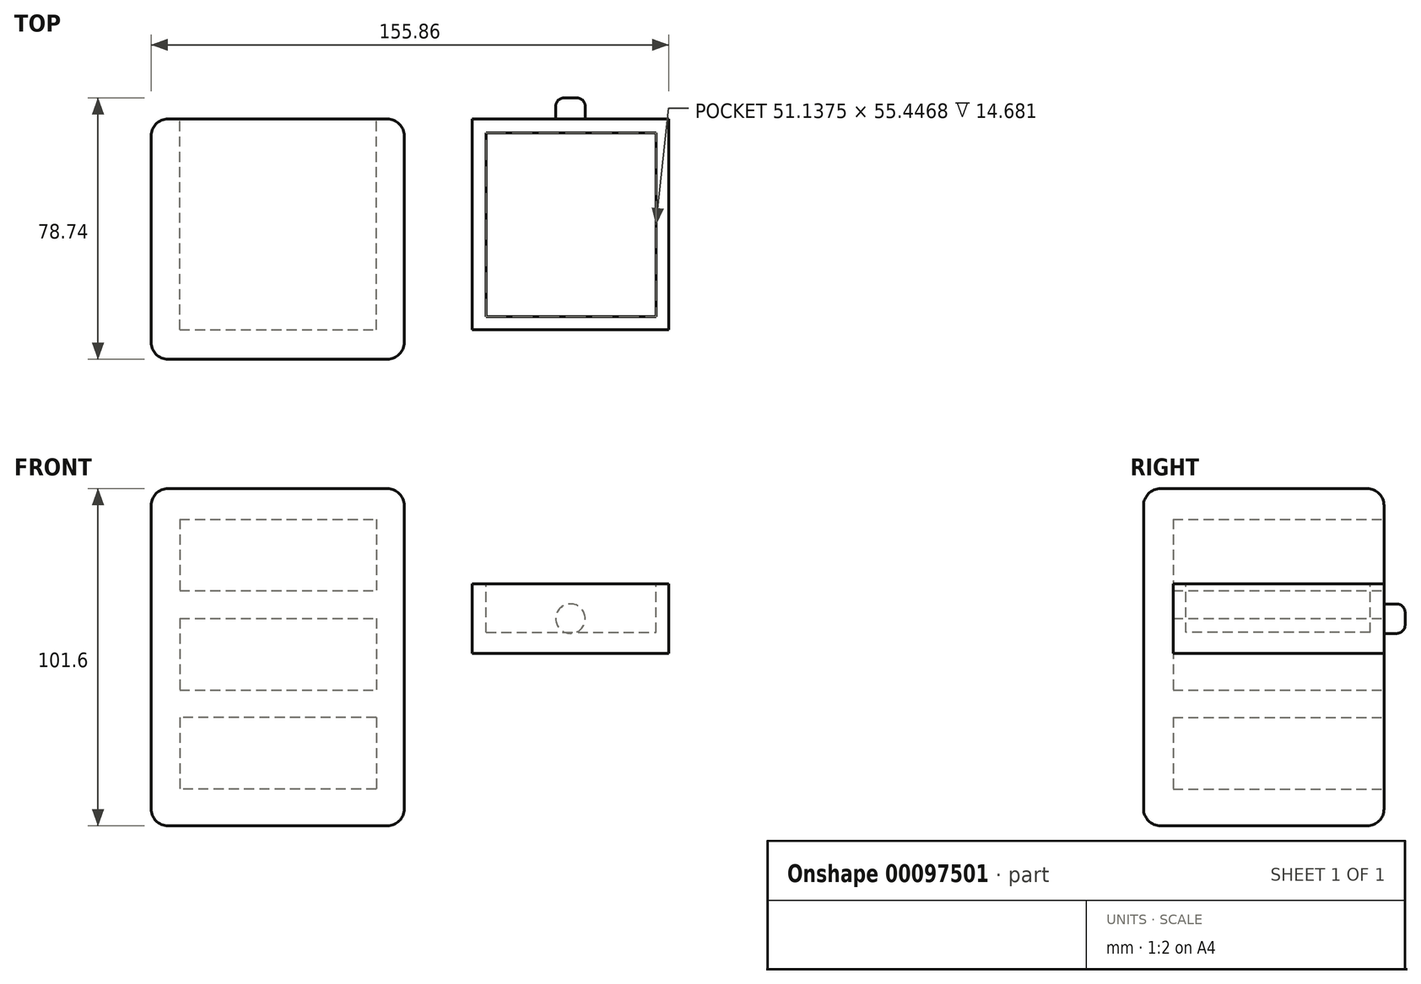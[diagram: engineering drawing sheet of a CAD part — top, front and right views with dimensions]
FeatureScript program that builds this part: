
annotation { "Feature Type Name" : "Feature", "Feature Type Description" : "" }
export const myFeature = defineFeature(function(context is Context, id is Id, definition is map)
    precondition{}
    {
        {
            var Q0;
            Q0=qCreatedBy(makeId("Front.planeOp"),FACE);
            var sketch = newSketch(context, id + "F0", { "sketchPlane" : qUnion([Q0])});
            skLineSegment(sketch, "E0.bottom", {"start": v(-38.24, 55.06) * mm, "end": v(37.96, 55.06) * mm});
            skLineSegment(sketch, "E0.top", {"start": v(-38.24, -46.54) * mm, "end": v(37.96, -46.54) * mm});
            skLineSegment(sketch, "E0.left", {"start": v(-38.24, 55.06) * mm, "end": v(-38.24, -46.54) * mm});
            skLineSegment(sketch, "E0.right", {"start": v(37.96, 55.06) * mm, "end": v(37.96, -46.54) * mm});
            skLineSegment(sketch, "E1.bottom", {"start": v(-29.6, 45.82) * mm, "end": v(29.6, 45.82) * mm});
            skLineSegment(sketch, "E1.top", {"start": v(-29.6, 24.28) * mm, "end": v(29.6, 24.28) * mm});
            skLineSegment(sketch, "E1.left", {"start": v(-29.6, 45.82) * mm, "end": v(-29.6, 24.28) * mm});
            skLineSegment(sketch, "E1.right", {"start": v(29.6, 45.82) * mm, "end": v(29.6, 24.28) * mm});
            skLineSegment(sketch, "E2.bottom", {"start": v(-29.6, 15.94) * mm, "end": v(29.6, 15.94) * mm});
            skLineSegment(sketch, "E2.top", {"start": v(-29.6, -5.6) * mm, "end": v(29.6, -5.6) * mm});
            skLineSegment(sketch, "E2.left", {"start": v(-29.6, 15.94) * mm, "end": v(-29.6, -5.6) * mm});
            skLineSegment(sketch, "E2.right", {"start": v(29.6, 15.94) * mm, "end": v(29.6, -5.6) * mm});
            skLineSegment(sketch, "E3.bottom", {"start": v(29.6, -13.93) * mm, "end": v(-29.6, -13.93) * mm});
            skLineSegment(sketch, "E3.top", {"start": v(29.6, -35.48) * mm, "end": v(-29.6, -35.48) * mm});
            skLineSegment(sketch, "E3.left", {"start": v(29.6, -13.93) * mm, "end": v(29.6, -35.48) * mm});
            skLineSegment(sketch, "E3.right", {"start": v(-29.6, -13.93) * mm, "end": v(-29.6, -35.48) * mm});
            skSolve(sketch);
        }
        {
            var Q0;
            Q0=makeQuery(id+"F0.imprint","IMPRINT",FACE,{"disambiguationData":[TD([[makeQuery(id+"F0.imprint","IMPRINT",EDGE,{"derivedFrom":sQuery(id+"F0.wireOp",EDGE,"E0.bottom")}),-1.0]])]});
            extrude(context, id + "F1", {"entities" : qUnion([Q0]), "depth" : 63.5 * mm});
        }
        {
            var Q0;
            Q0=makeQuery(id+"F1.opExtrude","CAP_FACE",FACE,{"disambiguationData":[OSD([sQuery(id+"F0.wireOp",EDGE,"E0.bottom"),sQuery(id+"F0.wireOp",EDGE,"E0.top"),sQuery(id+"F0.wireOp",EDGE,"E0.left"),sQuery(id+"F0.wireOp",EDGE,"E0.right"),sQuery(id+"F0.wireOp",EDGE,"E1.bottom"),sQuery(id+"F0.wireOp",EDGE,"E1.top"),sQuery(id+"F0.wireOp",EDGE,"E1.left"),sQuery(id+"F0.wireOp",EDGE,"E1.right"),sQuery(id+"F0.wireOp",EDGE,"E2.bottom"),sQuery(id+"F0.wireOp",EDGE,"E2.top"),sQuery(id+"F0.wireOp",EDGE,"E2.left"),sQuery(id+"F0.wireOp",EDGE,"E2.right"),sQuery(id+"F0.wireOp",EDGE,"E3.bottom"),sQuery(id+"F0.wireOp",EDGE,"E3.top"),sQuery(id+"F0.wireOp",EDGE,"E3.left"),sQuery(id+"F0.wireOp",EDGE,"E3.right")])],"isStart":false});
            var sketch = newSketch(context, id + "F2", { "sketchPlane" : qUnion([Q0])});
            skLineSegment(sketch, "E4.bottom", {"start": v(-38.24, 55.06) * mm, "end": v(37.96, 55.06) * mm});
            skLineSegment(sketch, "E4.top", {"start": v(-38.24, -46.54) * mm, "end": v(37.96, -46.54) * mm});
            skLineSegment(sketch, "E4.left", {"start": v(-38.24, 55.06) * mm, "end": v(-38.24, -46.54) * mm});
            skLineSegment(sketch, "E4.right", {"start": v(37.96, 55.06) * mm, "end": v(37.96, -46.54) * mm});
            skSolve(sketch);
        }
        {
            var Q0;
            Q0 = qSketchRegion(id + "F2", true);
            extrude(context, id + "F3", {"entities" : qUnion([Q0]), "operationType" : NewBodyOperationType.ADD, "depth" : 8.9 * mm});
        }
        {
            var Q0;
            Q0=qCreatedBy(makeId("Front.planeOp"),FACE);
            var sketch = newSketch(context, id + "F4", { "sketchPlane" : qUnion([Q0])});
            skLineSegment(sketch, "E5.bottom", {"start": v(58.43, 26.4) * mm, "end": v(117.62, 26.4) * mm});
            skLineSegment(sketch, "E5.top", {"start": v(58.43, 5.37) * mm, "end": v(117.62, 5.37) * mm});
            skLineSegment(sketch, "E5.left", {"start": v(58.43, 26.4) * mm, "end": v(58.43, 5.37) * mm});
            skLineSegment(sketch, "E5.right", {"start": v(117.62, 26.4) * mm, "end": v(117.62, 5.37) * mm});
            skSolve(sketch);
        }
        {
            var Q0;
            Q0=makeQuery(id+"F4.imprint","IMPRINT",FACE,{"disambiguationData":[TD([[makeQuery(id+"F4.imprint","IMPRINT",EDGE,{"derivedFrom":sQuery(id+"F4.wireOp",EDGE,"E5.bottom")}),-1.0]])]});
            extrude(context, id + "F5", {"entities" : qUnion([Q0]), "depth" : 63.5 * mm});
        }
        {
            var Q0;
            Q0=makeQuery(id+"F5.opExtrude","CAP_FACE",FACE,{"disambiguationData":[OSD([sQuery(id+"F4.wireOp",EDGE,"E5.bottom"),sQuery(id+"F4.wireOp",EDGE,"E5.top"),sQuery(id+"F4.wireOp",EDGE,"E5.left"),sQuery(id+"F4.wireOp",EDGE,"E5.right")])],"isStart":true});
            var Q1;
            Q1=makeQuery(id+"F5.opExtrude","SWEPT_BODY",BODY,{"disambiguationData":[OSD([sQuery(id+"F4.wireOp",EDGE,"E5.bottom"),sQuery(id+"F4.wireOp",EDGE,"E5.top"),sQuery(id+"F4.wireOp",EDGE,"E5.left"),sQuery(id+"F4.wireOp",EDGE,"E5.right")])]});
            shell(context, id + "F6", {"isHollow" : true, "entities" : qUnion([Q0]), "parts" : qUnion([Q1]), "thickness" : 6.35 * mm});
        }
        {
            var Q0;
            Q0=makeQuery(id+"F5.opExtrude","SWEPT_FACE",FACE,{"disambiguationData":[OSD([sQuery(id+"F4.wireOp",EDGE,"E5.bottom")])]});
            var sketch = newSketch(context, id + "F7", { "sketchPlane" : qUnion([Q0])});
            skLineSegment(sketch, "E6.bottom", {"start": v(62.65, -4.17) * mm, "end": v(113.79, -4.17) * mm});
            skLineSegment(sketch, "E6.top", {"start": v(62.65, -59.61) * mm, "end": v(113.79, -59.61) * mm});
            skLineSegment(sketch, "E6.left", {"start": v(62.65, -4.17) * mm, "end": v(62.65, -59.61) * mm});
            skLineSegment(sketch, "E6.right", {"start": v(113.79, -4.17) * mm, "end": v(113.79, -59.61) * mm});
            skSolve(sketch);
        }
        {
            var Q0;
            Q0 = qSketchRegion(id + "F7", true);
            extrude(context, id + "F8", {"entities" : qUnion([Q0]), "operationType" : NewBodyOperationType.REMOVE, "oppositeDirection" : true, "depth" : 14.68 * mm});
        }
        {
            var Q0;
            Q0=makeQuery(id+"F5.opExtrude","CAP_FACE",FACE,{"disambiguationData":[OSD([sQuery(id+"F4.wireOp",EDGE,"E5.bottom"),sQuery(id+"F4.wireOp",EDGE,"E5.top"),sQuery(id+"F4.wireOp",EDGE,"E5.left"),sQuery(id+"F4.wireOp",EDGE,"E5.right")])],"isStart":true});
            var sketch = newSketch(context, id + "F9", { "sketchPlane" : qUnion([Q0])});
            skCircle(sketch, "E7", {"center": v(-88.02, 15.88) * mm, "radius": 4.45 * mm});
            skPoint(sketch, "E7.centerSnap0", {"position": v(-88.02, 5.37) * mm});
            skPoint(sketch, "E7.centerSnap1", {"position": v(-58.43, 15.88) * mm});
            skSolve(sketch);
        }
        {
            var Q0;
            Q0 = qSketchRegion(id + "F9", true);
            extrude(context, id + "F10", {"entities" : qUnion([Q0]), "operationType" : NewBodyOperationType.ADD, "depth" : 6.35 * mm});
        }
        {
            var Q0;
            Q0=makeQuery(id+"F10.opExtrude","CAP_EDGE",EDGE,{"disambiguationData":[OSD([sQuery(id+"F9.wireOp",EDGE,"E7")])],"isStart":false});
            fillet(context, id + "F11", {"entities" : qUnion([Q0]), "radius" : 2.54 * mm, "tangentPropagation" : true, "allowEdgeOverflow" : false});
        }
        {
            var Q0;
            Q0=makeQuery(id+"F1.opExtrude","CAP_EDGE",EDGE,{"disambiguationData":[OSD([sQuery(id+"F0.wireOp",EDGE,"E0.bottom")])],"isStart":true});
            var Q1;
            Q1=makeQuery(id+"F1.opExtrude","CAP_EDGE",EDGE,{"disambiguationData":[OSD([sQuery(id+"F0.wireOp",EDGE,"E0.left")])],"isStart":true});
            var Q2;
            Q2=makeQuery(id+"F1.opExtrude","CAP_EDGE",EDGE,{"disambiguationData":[OSD([sQuery(id+"F0.wireOp",EDGE,"E0.top")])],"isStart":true});
            var Q3;
            Q3=makeQuery(id+"F1.opExtrude","CAP_EDGE",EDGE,{"disambiguationData":[OSD([sQuery(id+"F0.wireOp",EDGE,"E0.right")])],"isStart":true});
            var Q4;
            Q4=makeQuery(id+"F3.boolean.opBoolean","MERGE",EDGE,{"derivedFrom":[makeQuery(id+"F1.opExtrude","SWEPT_EDGE",EDGE,{"disambiguationData":[OSD([sQuery(id+"F0.wireOp",EDGE,"E0.bottom"),sQuery(id+"F0.wireOp",EDGE,"E0.left")])]}),makeQuery(id+"F3.opExtrude","SWEPT_EDGE",EDGE,{"disambiguationData":[OSD([sQuery(id+"F2.wireOp",EDGE,"E4.bottom"),sQuery(id+"F2.wireOp",EDGE,"E4.left")])]})]});
            var Q5;
            Q5=makeQuery(id+"F3.opExtrude","CAP_EDGE",EDGE,{"disambiguationData":[OSD([sQuery(id+"F2.wireOp",EDGE,"E4.left")])],"isStart":false});
            var Q6;
            Q6=makeQuery(id+"F3.boolean.opBoolean","MERGE",EDGE,{"derivedFrom":[makeQuery(id+"F1.opExtrude","SWEPT_EDGE",EDGE,{"disambiguationData":[OSD([sQuery(id+"F0.wireOp",EDGE,"E0.top"),sQuery(id+"F0.wireOp",EDGE,"E0.left")])]}),makeQuery(id+"F3.opExtrude","SWEPT_EDGE",EDGE,{"disambiguationData":[OSD([sQuery(id+"F2.wireOp",EDGE,"E4.top"),sQuery(id+"F2.wireOp",EDGE,"E4.left")])]})]});
            var Q7;
            Q7=makeQuery(id+"F3.boolean.opBoolean","MERGE",EDGE,{"derivedFrom":[makeQuery(id+"F1.opExtrude","SWEPT_EDGE",EDGE,{"disambiguationData":[OSD([sQuery(id+"F0.wireOp",EDGE,"E0.bottom"),sQuery(id+"F0.wireOp",EDGE,"E0.right")])]}),makeQuery(id+"F3.opExtrude","SWEPT_EDGE",EDGE,{"disambiguationData":[OSD([sQuery(id+"F2.wireOp",EDGE,"E4.bottom"),sQuery(id+"F2.wireOp",EDGE,"E4.right")])]})]});
            var Q8;
            Q8=makeQuery(id+"F3.opExtrude","CAP_EDGE",EDGE,{"disambiguationData":[OSD([sQuery(id+"F2.wireOp",EDGE,"E4.right")])],"isStart":false});
            var Q9;
            Q9=makeQuery(id+"F3.boolean.opBoolean","MERGE",EDGE,{"derivedFrom":[makeQuery(id+"F1.opExtrude","SWEPT_EDGE",EDGE,{"disambiguationData":[OSD([sQuery(id+"F0.wireOp",EDGE,"E0.top"),sQuery(id+"F0.wireOp",EDGE,"E0.right")])]}),makeQuery(id+"F3.opExtrude","SWEPT_EDGE",EDGE,{"disambiguationData":[OSD([sQuery(id+"F2.wireOp",EDGE,"E4.top"),sQuery(id+"F2.wireOp",EDGE,"E4.right")])]})]});
            var Q10;
            Q10=makeQuery(id+"F3.opExtrude","CAP_EDGE",EDGE,{"disambiguationData":[OSD([sQuery(id+"F2.wireOp",EDGE,"E4.bottom")])],"isStart":false});
            var Q11;
            Q11=makeQuery(id+"F3.opExtrude","CAP_EDGE",EDGE,{"disambiguationData":[OSD([sQuery(id+"F2.wireOp",EDGE,"E4.top")])],"isStart":false});
            fillet(context, id + "F12", {"entities" : qUnion([Q0, Q1, Q2, Q3, Q4, Q5, Q6, Q7, Q8, Q9, Q10, Q11]), "radius" : 5.08 * mm, "tangentPropagation" : true, "allowEdgeOverflow" : false});
        }
    });
